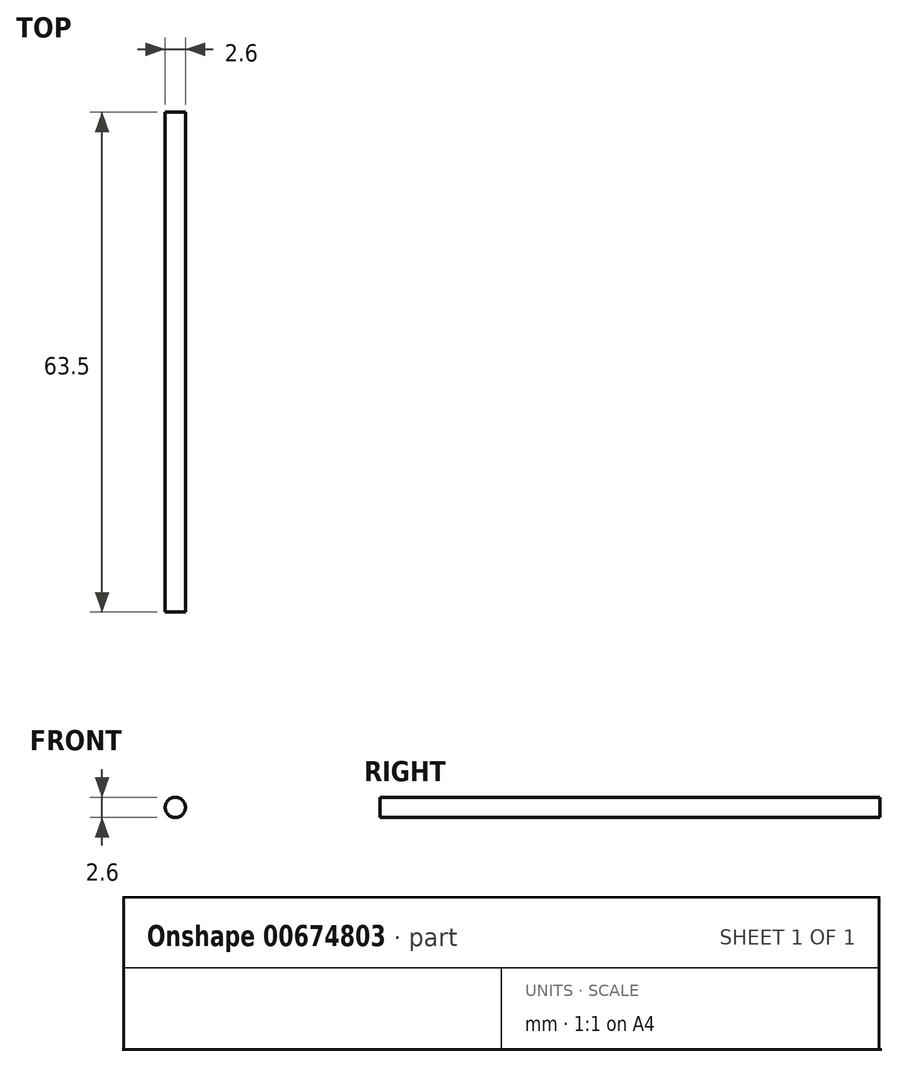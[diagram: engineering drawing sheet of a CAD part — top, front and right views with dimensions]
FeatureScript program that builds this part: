
annotation { "Feature Type Name" : "Feature", "Feature Type Description" : "" }
export const myFeature = defineFeature(function(context is Context, id is Id, definition is map)
    precondition{}
    {
        {
            var Q0;
            Q0=qCreatedBy(makeId("Front.planeOp"),FACE);
            var sketch = newSketch(context, id + "F0", { "sketchPlane" : qUnion([Q0])});
            skCircle(sketch, "E0", {"center": v(0, 0) * mm, "radius": 1.3 * mm});
            skSolve(sketch);
        }
        {
            var Q0;
            Q0 = qSketchRegion(id + "F0", true);
            extrude(context, id + "F1", {"entities" : qUnion([Q0]), "depth" : 63.5 * mm, "offsetDistance" : 25.4 * mm});
        }
    });
